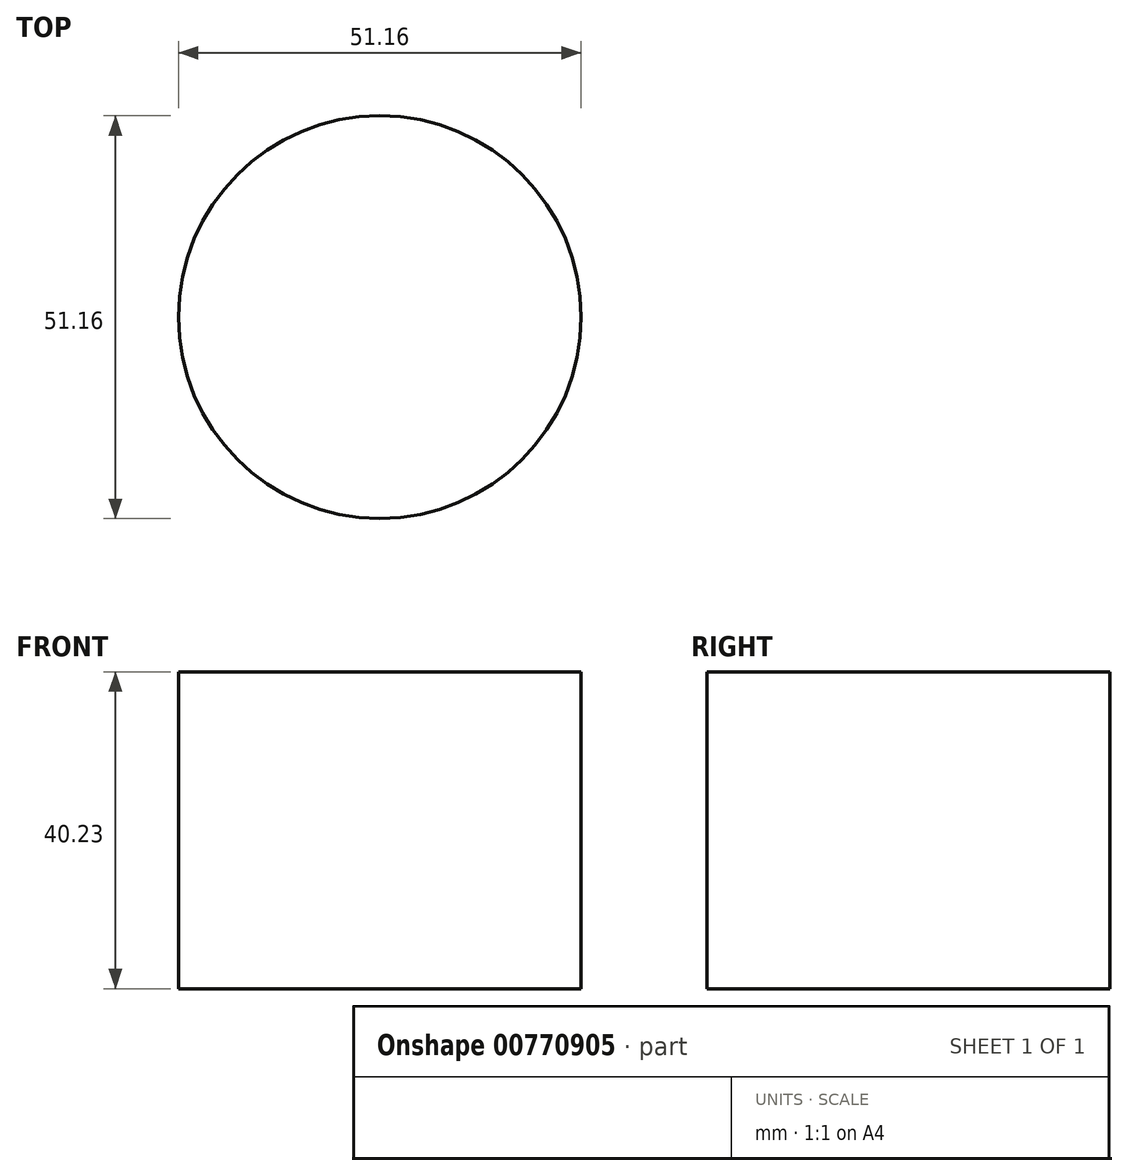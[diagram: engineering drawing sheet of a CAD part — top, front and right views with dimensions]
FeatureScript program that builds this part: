
annotation { "Feature Type Name" : "Feature", "Feature Type Description" : "" }
export const myFeature = defineFeature(function(context is Context, id is Id, definition is map)
    precondition{}
    {
        {
            var Q0;
            Q0=qCreatedBy(makeId("Top.planeOp"),FACE);
            var sketch = newSketch(context, id + "F0", { "sketchPlane" : qUnion([Q0])});
            skCircle(sketch, "E0", {"center": v(0, 0) * mm, "radius": 25.58 * mm});
            skSolve(sketch);
        }
        {
            var Q0;
            Q0=makeQuery(id+"F0.imprint","IMPRINT",FACE,{"disambiguationData":[TD([[makeQuery(id+"F0.imprint","IMPRINT",EDGE,{"derivedFrom":sQuery(id+"F0.wireOp",EDGE,"E0")}),1.0]])]});
            extrude(context, id + "F1", {"entities" : qUnion([Q0]), "depth" : 40.23 * mm, "offsetDistance" : 25.4 * mm});
        }
    });
